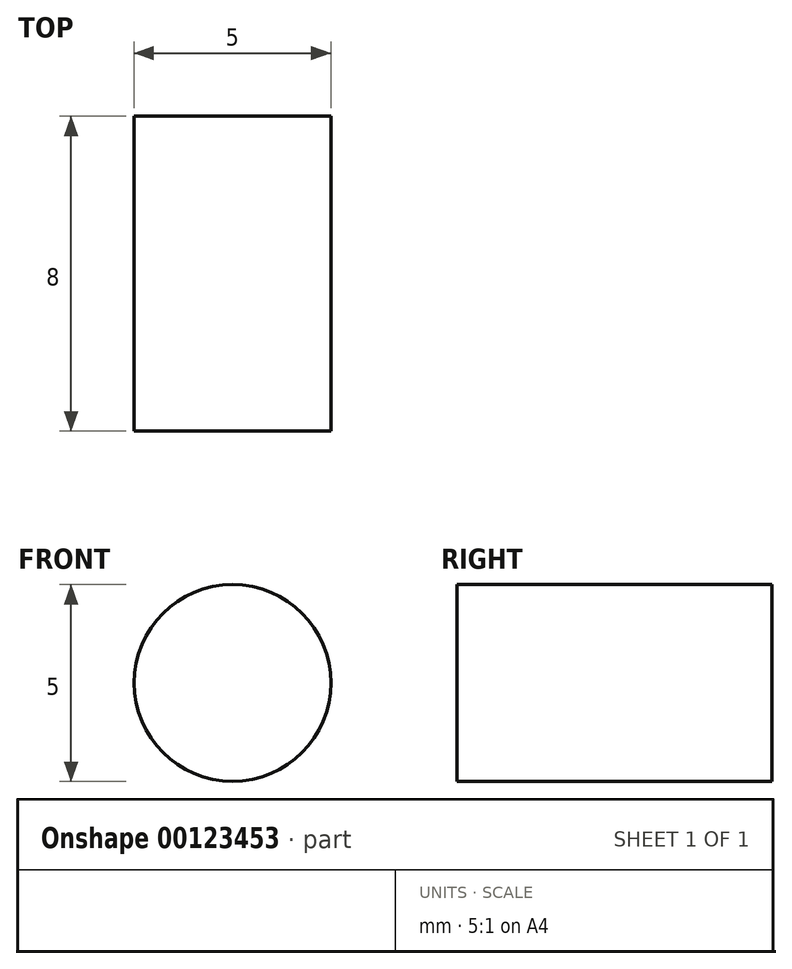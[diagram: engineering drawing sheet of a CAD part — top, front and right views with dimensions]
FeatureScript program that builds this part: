
annotation { "Feature Type Name" : "Feature", "Feature Type Description" : "" }
export const myFeature = defineFeature(function(context is Context, id is Id, definition is map)
    precondition{}
    {
        {
            var Q0;
            Q0=qCreatedBy(makeId("Front.planeOp"),FACE);
            var sketch = newSketch(context, id + "F0", { "sketchPlane" : qUnion([Q0])});
            skCircle(sketch, "E0", {"center": v(0, 0) * mm, "radius": 2.5 * mm});
            skSolve(sketch);
        }
        {
            var Q0;
            Q0=makeQuery(id+"F0.imprint","IMPRINT",FACE,{"disambiguationData":[TD([[makeQuery(id+"F0.imprint","IMPRINT",EDGE,{"derivedFrom":sQuery(id+"F0.wireOp",EDGE,"E0")}),1.0]])]});
            extrude(context, id + "F1", {"entities" : qUnion([Q0]), "endBound" : BoundingType.SYMMETRIC, "depth" : 8 * mm});
        }
    });
